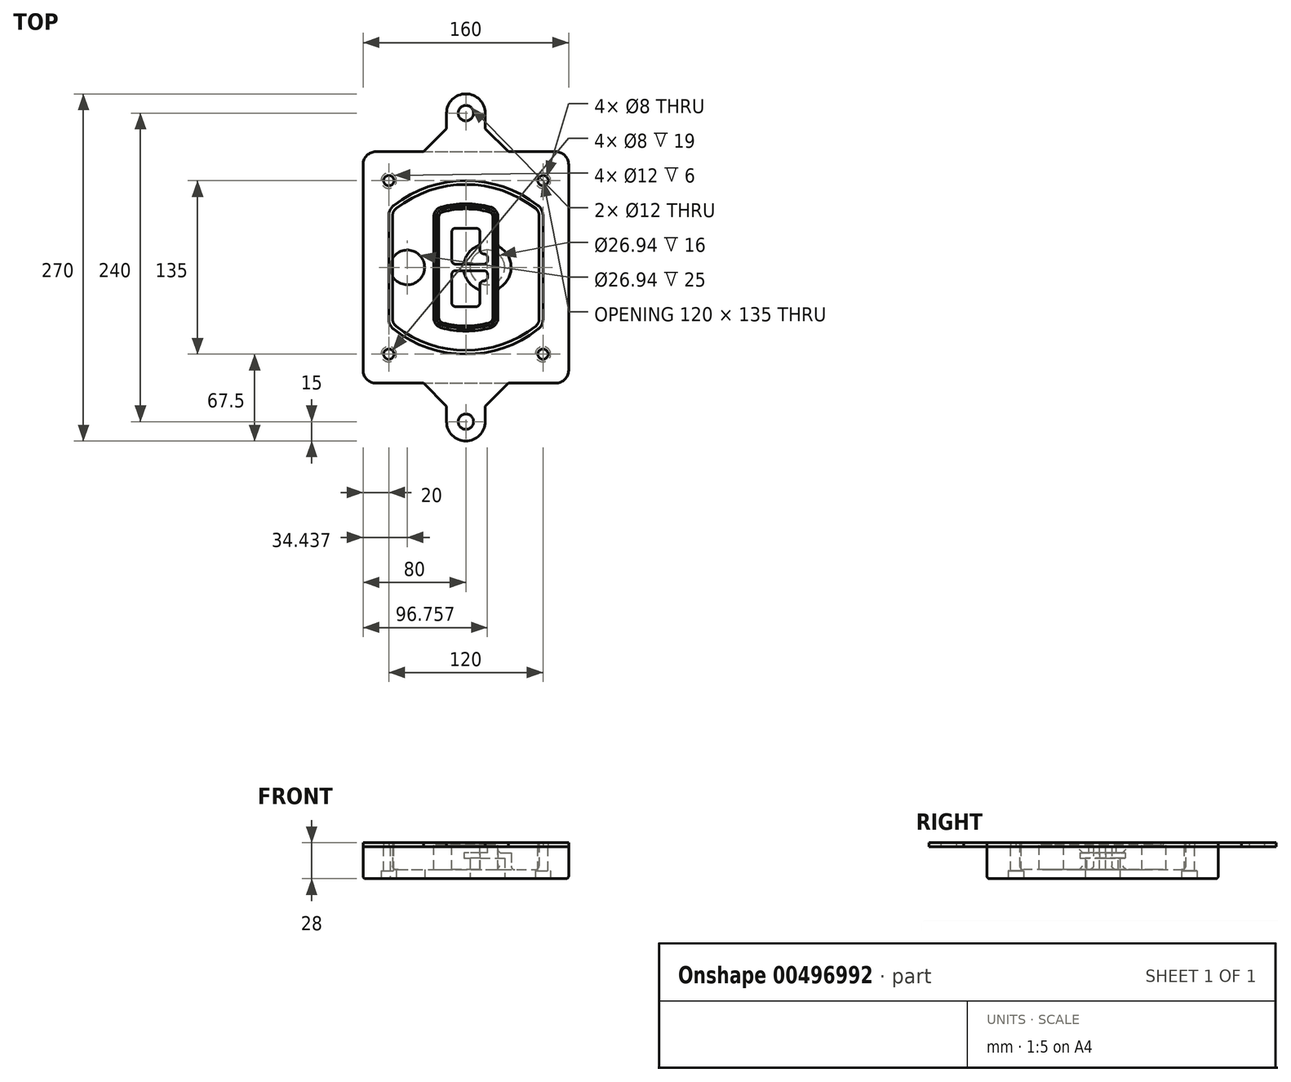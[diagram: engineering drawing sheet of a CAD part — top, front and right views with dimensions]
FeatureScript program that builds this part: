
annotation { "Feature Type Name" : "Feature", "Feature Type Description" : "" }
export const myFeature = defineFeature(function(context is Context, id is Id, definition is map)
    precondition{}
    {
        {
            var Q0;
            Q0=qCreatedBy(makeId("Top.planeOp"),FACE);
            var sketch = newSketch(context, id + "F0", { "sketchPlane" : qUnion([Q0])});
            skPoint(sketch, "E0.rect.middle", {"position": v(0, 0) * mm});
            skLineSegment(sketch, "E1.bottom", {"start": v(-70, -90) * mm, "end": v(70, -90) * mm});
            skLineSegment(sketch, "E1.top", {"start": v(-70, 90) * mm, "end": v(70, 90) * mm});
            skLineSegment(sketch, "E1.left", {"start": v(-80, -80) * mm, "end": v(-80, 80) * mm});
            skLineSegment(sketch, "E1.right", {"start": v(80, -80) * mm, "end": v(80, 80) * mm});
            skLineSegment(sketch, "E2", {"start": v(-80, 90) * mm, "end": v(80, -90) * mm, "construction": true});
            skLineSegment(sketch, "E3", {"start": v(80, 90) * mm, "end": v(-80, -90) * mm, "construction": true});
            skCircle(sketch, "E4", {"center": v(-60, 67.5) * mm, "radius": 4 * mm});
            skCircle(sketch, "E5", {"center": v(60, 67.5) * mm, "radius": 4 * mm});
            skCircle(sketch, "E6", {"center": v(60, -67.5) * mm, "radius": 4 * mm});
            skCircle(sketch, "E7", {"center": v(-60, -67.5) * mm, "radius": 4 * mm});
            skLineSegment(sketch, "E8", {"start": v(-60, 67.5) * mm, "end": v(60, 67.5) * mm, "construction": true});
            skLineSegment(sketch, "E9", {"start": v(60, 67.5) * mm, "end": v(60, -67.5) * mm, "construction": true});
            skLineSegment(sketch, "E10", {"start": v(60, -67.5) * mm, "end": v(-60, -67.5) * mm, "construction": true});
            skLineSegment(sketch, "E11", {"start": v(-60, -67.5) * mm, "end": v(-60, 67.5) * mm, "construction": true});
            skLineSegment(sketch, "E12", {"start": v(-60, 40.3) * mm, "end": v(-60, -40.3) * mm});
            skLineSegment(sketch, "E13", {"start": v(60, 40.3) * mm, "end": v(60, -40.3) * mm});
            skArc(sketch, "E14", {"start": v(56.15, 48.18) * mm, "mid": v(0, 67.5) * mm, "end": v(-56.15, 48.18) * mm});
            skArc(sketch, "E15", {"start": v(-56.15, -48.18) * mm, "mid": v(0, -67.5) * mm, "end": v(56.15, -48.18) * mm});
            skLineSegment(sketch, "E16", {"start": v(-60, 0) * mm, "end": v(60, 0) * mm, "construction": true});
            skPoint(sketch, "E17.visualSharp", {"position": v(-60, -45) * mm});
            skArc(sketch, "E17.filletArc", {"start": v(-60, -40.3) * mm, "mid": v(-58.99, -44.68) * mm, "end": v(-56.15, -48.18) * mm});
            skPoint(sketch, "E18.visualSharp", {"position": v(-60, 45) * mm});
            skArc(sketch, "E18.filletArc", {"start": v(-56.15, 48.18) * mm, "mid": v(-58.99, 44.68) * mm, "end": v(-60, 40.3) * mm});
            skPoint(sketch, "E19.visualSharp", {"position": v(60, 45) * mm});
            skArc(sketch, "E19.filletArc", {"start": v(60, 40.3) * mm, "mid": v(58.99, 44.68) * mm, "end": v(56.15, 48.18) * mm});
            skPoint(sketch, "E20.visualSharp", {"position": v(60, -45) * mm});
            skArc(sketch, "E20.filletArc", {"start": v(56.15, -48.18) * mm, "mid": v(58.99, -44.68) * mm, "end": v(60, -40.3) * mm});
            skPoint(sketch, "E21.visualSharp", {"position": v(-80, 90) * mm});
            skArc(sketch, "E21.filletArc", {"start": v(-70, 90) * mm, "mid": v(-77.07, 87.07) * mm, "end": v(-80, 80) * mm});
            skPoint(sketch, "E22.visualSharp", {"position": v(80, 90) * mm});
            skArc(sketch, "E22.filletArc", {"start": v(80, 80) * mm, "mid": v(77.07, 87.07) * mm, "end": v(70, 90) * mm});
            skPoint(sketch, "E23.visualSharp", {"position": v(80, -90) * mm});
            skArc(sketch, "E23.filletArc", {"start": v(70, -90) * mm, "mid": v(77.07, -87.07) * mm, "end": v(80, -80) * mm});
            skPoint(sketch, "E24.visualSharp", {"position": v(-80, -90) * mm});
            skArc(sketch, "E24.filletArc", {"start": v(-80, -80) * mm, "mid": v(-77.07, -87.07) * mm, "end": v(-70, -90) * mm});
            skArc(sketch, "E25.0", {"start": v(57, 40.3) * mm, "mid": v(56.3, 43.36) * mm, "end": v(54.3, 45.81) * mm});
            skLineSegment(sketch, "E25.1", {"start": v(57, 40.3) * mm, "end": v(57, -40.3) * mm});
            skArc(sketch, "E25.2", {"start": v(54.3, -45.81) * mm, "mid": v(56.3, -43.36) * mm, "end": v(57, -40.3) * mm});
            skArc(sketch, "E25.3", {"start": v(-54.3, -45.81) * mm, "mid": v(0, -64.5) * mm, "end": v(54.3, -45.81) * mm});
            skArc(sketch, "E25.4", {"start": v(-57, -40.3) * mm, "mid": v(-56.3, -43.36) * mm, "end": v(-54.3, -45.81) * mm});
            skArc(sketch, "E25.5", {"start": v(54.3, 45.81) * mm, "mid": v(0, 64.5) * mm, "end": v(-54.3, 45.81) * mm});
            skLineSegment(sketch, "E25.6", {"start": v(-57, 40.3) * mm, "end": v(-57, -40.3) * mm});
            skArc(sketch, "E25.7", {"start": v(-54.3, 45.81) * mm, "mid": v(-56.3, 43.36) * mm, "end": v(-57, 40.3) * mm});
            skArc(sketch, "E26.0", {"start": v(-58.62, 51.33) * mm, "mid": v(-62.58, 46.43) * mm, "end": v(-64, 40.3) * mm});
            skArc(sketch, "E26.1", {"start": v(58.62, 51.33) * mm, "mid": v(0, 71.5) * mm, "end": v(-58.62, 51.33) * mm});
            skArc(sketch, "E26.2", {"start": v(64, 40.3) * mm, "mid": v(62.58, 46.43) * mm, "end": v(58.62, 51.33) * mm});
            skLineSegment(sketch, "E26.3", {"start": v(64, 40.3) * mm, "end": v(64, -40.3) * mm});
            skArc(sketch, "E26.4", {"start": v(58.62, -51.33) * mm, "mid": v(62.58, -46.43) * mm, "end": v(64, -40.3) * mm});
            skLineSegment(sketch, "E26.5", {"start": v(-64, 40.3) * mm, "end": v(-64, -40.3) * mm});
            skArc(sketch, "E26.6", {"start": v(-58.62, -51.33) * mm, "mid": v(0, -71.5) * mm, "end": v(58.62, -51.33) * mm});
            skArc(sketch, "E26.7", {"start": v(-64, -40.3) * mm, "mid": v(-62.58, -46.43) * mm, "end": v(-58.62, -51.33) * mm});
            skSolve(sketch);
        }
        {
            var Q0;
            Q0=makeQuery(id+"F0.imprint","IMPRINT",FACE,{"disambiguationData":[TD([[makeQuery(id+"F0.imprint","IMPRINT",EDGE,{"derivedFrom":sQuery(id+"F0.wireOp",EDGE,"E1.bottom")}),1.0]])]});
            var Q1;
            Q1=makeQuery(id+"F0.imprint","IMPRINT",FACE,{"disambiguationData":[TD([[makeQuery(id+"F0.imprint","IMPRINT",EDGE,{"derivedFrom":sQuery(id+"F0.wireOp",EDGE,"E12")}),1.0]])]});
            var Q2;
            Q2=makeQuery(id+"F0.imprint","IMPRINT",FACE,{"disambiguationData":[TD([[makeQuery(id+"F0.imprint","IMPRINT",EDGE,{"derivedFrom":sQuery(id+"F0.wireOp",EDGE,"E25.0")}),1.0]])]});
            var Q3;
            Q3=makeQuery(id+"F0.imprint","IMPRINT",FACE,{"disambiguationData":[TD([[makeQuery(id+"F0.imprint","IMPRINT",EDGE,{"derivedFrom":sQuery(id+"F0.wireOp",EDGE,"E12")}),-1.0]])]});
            extrude(context, id + "F1", {"entities" : qUnion([Q0, Q1, Q2, Q3]), "oppositeDirection" : true, "depth" : 25 * mm});
        }
        {
            var Q0;
            Q0=makeQuery(id+"F0.imprint","IMPRINT",FACE,{"disambiguationData":[TD([[makeQuery(id+"F0.imprint","IMPRINT",EDGE,{"derivedFrom":sQuery(id+"F0.wireOp",EDGE,"E12")}),1.0]])]});
            extrude(context, id + "F2", {"entities" : qUnion([Q0]), "operationType" : NewBodyOperationType.ADD, "depth" : 3 * mm});
        }
        {
            var Q0;
            Q0=makeQuery(id+"F0.imprint","IMPRINT",FACE,{"disambiguationData":[TD([[makeQuery(id+"F0.imprint","IMPRINT",EDGE,{"derivedFrom":sQuery(id+"F0.wireOp",EDGE,"E25.0")}),1.0]])]});
            extrude(context, id + "F3", {"entities" : qUnion([Q0]), "operationType" : NewBodyOperationType.REMOVE, "oppositeDirection" : true, "depth" : 18 * mm});
        }
        {
            var Q0;
            Q0=makeQuery(id+"F2.opExtrude","CAP_FACE",FACE,{"disambiguationData":[OSD([sQuery(id+"F0.wireOp",EDGE,"E12"),sQuery(id+"F0.wireOp",EDGE,"E13"),sQuery(id+"F0.wireOp",EDGE,"E14"),sQuery(id+"F0.wireOp",EDGE,"E15"),sQuery(id+"F0.wireOp",EDGE,"E17.filletArc"),sQuery(id+"F0.wireOp",EDGE,"E18.filletArc"),sQuery(id+"F0.wireOp",EDGE,"E19.filletArc"),sQuery(id+"F0.wireOp",EDGE,"E20.filletArc"),sQuery(id+"F0.wireOp",EDGE,"E25.0"),sQuery(id+"F0.wireOp",EDGE,"E25.1"),sQuery(id+"F0.wireOp",EDGE,"E25.2"),sQuery(id+"F0.wireOp",EDGE,"E25.3"),sQuery(id+"F0.wireOp",EDGE,"E25.4"),sQuery(id+"F0.wireOp",EDGE,"E25.5"),sQuery(id+"F0.wireOp",EDGE,"E25.6"),sQuery(id+"F0.wireOp",EDGE,"E25.7")])],"isStart":false});
            var sketch = newSketch(context, id + "F4", { "sketchPlane" : qUnion([Q0])});
            skArc(sketch, "E27.0", {"start": v(-19.08, -46.97) * mm, "mid": v(0, -49.5) * mm, "end": v(19.08, -46.97) * mm});
            skArc(sketch, "E28.0", {"start": v(19.08, 46.97) * mm, "mid": v(0, 49.5) * mm, "end": v(-19.08, 46.97) * mm});
            skLineSegment(sketch, "E29", {"start": v(-25, 39.25) * mm, "end": v(-25, -39.25) * mm});
            skLineSegment(sketch, "E30", {"start": v(25, 39.25) * mm, "end": v(25, -39.25) * mm});
            skLineSegment(sketch, "E31", {"start": v(-25, 45.1) * mm, "end": v(25, 45.1) * mm, "construction": true});
            skLineSegment(sketch, "E32", {"start": v(-25, -45.1) * mm, "end": v(25, -45.1) * mm, "construction": true});
            skPoint(sketch, "E33.visualSharp", {"position": v(-25, 45.1) * mm});
            skArc(sketch, "E33.filletArc", {"start": v(-19.08, 46.97) * mm, "mid": v(-23.35, 44.11) * mm, "end": v(-25, 39.25) * mm});
            skPoint(sketch, "E34.visualSharp", {"position": v(25, 45.1) * mm});
            skArc(sketch, "E34.filletArc", {"start": v(25, 39.25) * mm, "mid": v(23.35, 44.11) * mm, "end": v(19.08, 46.97) * mm});
            skPoint(sketch, "E35.visualSharp", {"position": v(25, -45.1) * mm});
            skArc(sketch, "E35.filletArc", {"start": v(19.08, -46.97) * mm, "mid": v(23.35, -44.11) * mm, "end": v(25, -39.25) * mm});
            skPoint(sketch, "E36.visualSharp", {"position": v(-25, -45.1) * mm});
            skArc(sketch, "E36.filletArc", {"start": v(-25, -39.25) * mm, "mid": v(-23.35, -44.11) * mm, "end": v(-19.08, -46.97) * mm});
            skArc(sketch, "E37.0", {"start": v(54.3, 45.81) * mm, "mid": v(0, 64.5) * mm, "end": v(-54.3, 45.81) * mm});
            skArc(sketch, "E37.1", {"start": v(-54.3, 45.81) * mm, "mid": v(-56.3, 43.36) * mm, "end": v(-57, 40.3) * mm});
            skLineSegment(sketch, "E37.2", {"start": v(-57, 40.3) * mm, "end": v(-57, -40.3) * mm});
            skArc(sketch, "E37.3", {"start": v(-57, -40.3) * mm, "mid": v(-56.3, -43.36) * mm, "end": v(-54.3, -45.81) * mm});
            skArc(sketch, "E37.4", {"start": v(-54.3, -45.81) * mm, "mid": v(0, -64.5) * mm, "end": v(54.3, -45.81) * mm});
            skArc(sketch, "E37.5", {"start": v(54.3, -45.81) * mm, "mid": v(56.3, -43.36) * mm, "end": v(57, -40.3) * mm});
            skLineSegment(sketch, "E37.6", {"start": v(57, 40.3) * mm, "end": v(57, -40.3) * mm});
            skArc(sketch, "E37.7", {"start": v(57, 40.3) * mm, "mid": v(56.3, 43.36) * mm, "end": v(54.3, 45.81) * mm});
            skLineSegment(sketch, "E38.0", {"start": v(23, 39.25) * mm, "end": v(23, -39.25) * mm});
            skArc(sketch, "E38.1", {"start": v(18.56, -45.04) * mm, "mid": v(21.76, -42.9) * mm, "end": v(23, -39.25) * mm});
            skArc(sketch, "E38.2", {"start": v(-18.56, -45.04) * mm, "mid": v(0, -47.5) * mm, "end": v(18.56, -45.04) * mm});
            skArc(sketch, "E38.3", {"start": v(-23, -39.25) * mm, "mid": v(-21.76, -42.9) * mm, "end": v(-18.56, -45.04) * mm});
            skLineSegment(sketch, "E38.4", {"start": v(-23, 39.25) * mm, "end": v(-23, -39.25) * mm});
            skArc(sketch, "E38.5", {"start": v(23, 39.25) * mm, "mid": v(21.76, 42.9) * mm, "end": v(18.56, 45.04) * mm});
            skArc(sketch, "E38.6", {"start": v(-18.56, 45.04) * mm, "mid": v(-21.76, 42.9) * mm, "end": v(-23, 39.25) * mm});
            skArc(sketch, "E38.7", {"start": v(18.56, 45.04) * mm, "mid": v(0, 47.5) * mm, "end": v(-18.56, 45.04) * mm});
            skArc(sketch, "E39.0", {"start": v(21, 39.25) * mm, "mid": v(20.18, 41.68) * mm, "end": v(18.04, 43.1) * mm});
            skLineSegment(sketch, "E39.1", {"start": v(21, 39.25) * mm, "end": v(21, -39.25) * mm});
            skArc(sketch, "E39.2", {"start": v(18.04, -43.1) * mm, "mid": v(20.18, -41.68) * mm, "end": v(21, -39.25) * mm});
            skArc(sketch, "E39.3", {"start": v(-18.04, -43.1) * mm, "mid": v(0, -45.5) * mm, "end": v(18.04, -43.1) * mm});
            skArc(sketch, "E39.4", {"start": v(-21, -39.25) * mm, "mid": v(-20.18, -41.68) * mm, "end": v(-18.04, -43.1) * mm});
            skArc(sketch, "E39.5", {"start": v(18.04, 43.1) * mm, "mid": v(0, 45.5) * mm, "end": v(-18.04, 43.1) * mm});
            skLineSegment(sketch, "E39.6", {"start": v(-21, 39.25) * mm, "end": v(-21, -39.25) * mm});
            skArc(sketch, "E39.7", {"start": v(-18.04, 43.1) * mm, "mid": v(-20.18, 41.68) * mm, "end": v(-21, 39.25) * mm});
            skLineSegment(sketch, "E40", {"start": v(-25, 0) * mm, "end": v(25, 0) * mm, "construction": true});
            skLineSegment(sketch, "E41", {"start": v(-11, 5.5) * mm, "end": v(-11, 27.5) * mm});
            skLineSegment(sketch, "E42", {"start": v(-8, 30.5) * mm, "end": v(8, 30.5) * mm});
            skLineSegment(sketch, "E43", {"start": v(11, 27.5) * mm, "end": v(11, 13.5) * mm});
            skLineSegment(sketch, "E44", {"start": v(14, 10.5) * mm, "end": v(14, 10.5) * mm});
            skLineSegment(sketch, "E45", {"start": v(17, 7.5) * mm, "end": v(17, 5.5) * mm});
            skLineSegment(sketch, "E46", {"start": v(14, 2.5) * mm, "end": v(-8, 2.5) * mm});
            skPoint(sketch, "E47.visualSharp", {"position": v(-11, 30.5) * mm});
            skArc(sketch, "E47.filletArc", {"start": v(-8, 30.5) * mm, "mid": v(-10.12, 29.62) * mm, "end": v(-11, 27.5) * mm});
            skPoint(sketch, "E48.visualSharp", {"position": v(11, 30.5) * mm});
            skArc(sketch, "E48.filletArc", {"start": v(11, 27.5) * mm, "mid": v(10.12, 29.62) * mm, "end": v(8, 30.5) * mm});
            skPoint(sketch, "E49.visualSharp", {"position": v(11, 10.5) * mm});
            skArc(sketch, "E49.filletArc", {"start": v(11, 13.5) * mm, "mid": v(11.88, 11.38) * mm, "end": v(14, 10.5) * mm});
            skPoint(sketch, "E50.visualSharp", {"position": v(17, 10.5) * mm});
            skArc(sketch, "E50.filletArc", {"start": v(17, 7.5) * mm, "mid": v(16.12, 9.62) * mm, "end": v(14, 10.5) * mm});
            skPoint(sketch, "E51.visualSharp", {"position": v(17, 2.5) * mm});
            skArc(sketch, "E51.filletArc", {"start": v(14, 2.5) * mm, "mid": v(16.12, 3.38) * mm, "end": v(17, 5.5) * mm});
            skPoint(sketch, "E52.visualSharp", {"position": v(-11, 2.5) * mm});
            skArc(sketch, "E52.filletArc", {"start": v(-11, 5.5) * mm, "mid": v(-10.12, 3.38) * mm, "end": v(-8, 2.5) * mm});
            skLineSegment(sketch, "E53.0.MirrorCS", {"start": v(14, -2.5) * mm, "end": v(-8, -2.5) * mm});
            skArc(sketch, "E54.0.MirrorCS", {"start": v(-11, -5.5) * mm, "mid": v(-10.12, -3.38) * mm, "end": v(-8, -2.5) * mm});
            skLineSegment(sketch, "E55.0.MirrorCS", {"start": v(-11, -5.5) * mm, "end": v(-11, -27.5) * mm});
            skArc(sketch, "E56.0.MirrorCS", {"start": v(-8, -30.5) * mm, "mid": v(-10.12, -29.62) * mm, "end": v(-11, -27.5) * mm});
            skLineSegment(sketch, "E57.0.MirrorCS", {"start": v(-8, -30.5) * mm, "end": v(8, -30.5) * mm});
            skArc(sketch, "E58.0.MirrorCS", {"start": v(11, -27.5) * mm, "mid": v(10.12, -29.62) * mm, "end": v(8, -30.5) * mm});
            skLineSegment(sketch, "E59.0.MirrorCS", {"start": v(11, -27.5) * mm, "end": v(11, -13.5) * mm});
            skArc(sketch, "E60.0.MirrorCS", {"start": v(11, -13.5) * mm, "mid": v(11.88, -11.38) * mm, "end": v(14, -10.5) * mm});
            skArc(sketch, "E61.0.MirrorCS", {"start": v(17, -7.5) * mm, "mid": v(16.12, -9.62) * mm, "end": v(14, -10.5) * mm});
            skLineSegment(sketch, "E62.0.MirrorCS", {"start": v(17, -7.5) * mm, "end": v(17, -5.5) * mm});
            skArc(sketch, "E63.0.MirrorCS", {"start": v(14, -2.5) * mm, "mid": v(16.12, -3.38) * mm, "end": v(17, -5.5) * mm});
            skSolve(sketch);
        }
        {
            var Q0;
            Q0=makeQuery(id+"F4.imprint","IMPRINT",FACE,{"disambiguationData":[TD([[makeQuery(id+"F4.imprint","IMPRINT",EDGE,{"derivedFrom":sQuery(id+"F4.wireOp",EDGE,"E27.0")}),1.0]])]});
            var Q1;
            Q1=makeQuery(id+"F4.imprint","IMPRINT",FACE,{"disambiguationData":[TD([[makeQuery(id+"F4.imprint","IMPRINT",EDGE,{"derivedFrom":sQuery(id+"F4.wireOp",EDGE,"E38.0")}),-1.0]])]});
            var Q2;
            Q2=makeQuery(id+"F4.imprint","IMPRINT",FACE,{"disambiguationData":[TD([[makeQuery(id+"F4.imprint","IMPRINT",EDGE,{"derivedFrom":sQuery(id+"F4.wireOp",EDGE,"E39.0")}),1.0]])]});
            extrude(context, id + "F5", {"entities" : qUnion([Q0, Q1, Q2]), "operationType" : NewBodyOperationType.ADD, "endBound" : BoundingType.UP_TO_NEXT, "oppositeDirection" : true, "depth" : 25 * mm});
        }
        {
            var Q0;
            Q0=makeQuery(id+"F4.imprint","IMPRINT",FACE,{"disambiguationData":[TD([[makeQuery(id+"F4.imprint","IMPRINT",EDGE,{"derivedFrom":sQuery(id+"F4.wireOp",EDGE,"E38.0")}),-1.0]])]});
            extrude(context, id + "F6", {"entities" : qUnion([Q0]), "operationType" : NewBodyOperationType.REMOVE, "oppositeDirection" : true, "depth" : 2 * mm});
        }
        {
            var Q0;
            Q0=makeQuery(id+"F1.opExtrude","CAP_FACE",FACE,{"disambiguationData":[OSD([sQuery(id+"F0.wireOp",EDGE,"E1.bottom"),sQuery(id+"F0.wireOp",EDGE,"E1.top"),sQuery(id+"F0.wireOp",EDGE,"E1.left"),sQuery(id+"F0.wireOp",EDGE,"E1.right"),sQuery(id+"F0.wireOp",EDGE,"E4"),sQuery(id+"F0.wireOp",EDGE,"E5"),sQuery(id+"F0.wireOp",EDGE,"E6"),sQuery(id+"F0.wireOp",EDGE,"E7"),sQuery(id+"F0.wireOp",EDGE,"E21.filletArc"),sQuery(id+"F0.wireOp",EDGE,"E22.filletArc"),sQuery(id+"F0.wireOp",EDGE,"E23.filletArc"),sQuery(id+"F0.wireOp",EDGE,"E24.filletArc")])],"isStart":false});
            var sketch = newSketch(context, id + "F7", { "sketchPlane" : qUnion([Q0])});
            skCircle(sketch, "E64", {"center": v(16.76, 0) * mm, "radius": 13.47 * mm});
            skCircle(sketch, "E65", {"center": v(-45.56, 0) * mm, "radius": 13.47 * mm});
            skLineSegment(sketch, "E66", {"start": v(80, 0) * mm, "end": v(-80, 0) * mm});
            skCircle(sketch, "E67", {"center": v(16.76, 0) * mm, "radius": 18.47 * mm});
            skCircle(sketch, "E68", {"center": v(60, -67.5) * mm, "radius": 6 * mm});
            skCircle(sketch, "E69", {"center": v(-60, -67.5) * mm, "radius": 6 * mm});
            skCircle(sketch, "E70", {"center": v(-60, 67.5) * mm, "radius": 6 * mm});
            skCircle(sketch, "E71", {"center": v(60, 67.5) * mm, "radius": 6 * mm});
            skSolve(sketch);
        }
        {
            var Q0;
            {var subQ1=sQuery(id+"F7.wireOp",EDGE,"E66");var subQ4=sQuery(id+"F7.wireOp",EDGE,"E64");var subQ6=makeQuery(id+"F7.imprint","INTERSECT",VERTEX,{"disambiguationData":[OD(0.0)],"derivedFrom":[subQ4,subQ1]});Q0=makeQuery(id+"F7.imprint","IMPRINT",FACE,{"disambiguationData":[TD([[makeQuery(id+"F7.imprint","IMPRINT",EDGE,{"disambiguationData":[TD([[subQ6,-1.0]])],"derivedFrom":subQ4}),-1.0]])]});}
            var Q1;
            {var subQ0=sQuery(id+"F7.wireOp",EDGE,"E66");var subQ1=sQuery(id+"F7.wireOp",EDGE,"E64");var subQ3=makeQuery(id+"F7.imprint","INTERSECT",VERTEX,{"disambiguationData":[OD(0.0)],"derivedFrom":[subQ1,subQ0]});Q1=makeQuery(id+"F7.imprint","IMPRINT",FACE,{"disambiguationData":[TD([[makeQuery(id+"F7.imprint","IMPRINT",EDGE,{"disambiguationData":[TD([[subQ3,-1.0]])],"derivedFrom":subQ1}),1.0]])]});}
            var Q2;
            {var subQ0=sQuery(id+"F7.wireOp",EDGE,"E66");var subQ1=sQuery(id+"F7.wireOp",EDGE,"E64");var subQ3=makeQuery(id+"F7.imprint","INTERSECT",VERTEX,{"disambiguationData":[OD(0.0)],"derivedFrom":[subQ1,subQ0]});Q2=makeQuery(id+"F7.imprint","IMPRINT",FACE,{"disambiguationData":[TD([[makeQuery(id+"F7.imprint","IMPRINT",EDGE,{"disambiguationData":[TD([[subQ3,1.0]])],"derivedFrom":subQ1}),1.0]])]});}
            var Q3;
            {var subQ1=sQuery(id+"F7.wireOp",EDGE,"E66");var subQ4=sQuery(id+"F7.wireOp",EDGE,"E64");var subQ6=makeQuery(id+"F7.imprint","INTERSECT",VERTEX,{"disambiguationData":[OD(0.0)],"derivedFrom":[subQ4,subQ1]});Q3=makeQuery(id+"F7.imprint","IMPRINT",FACE,{"disambiguationData":[TD([[makeQuery(id+"F7.imprint","IMPRINT",EDGE,{"disambiguationData":[TD([[subQ6,1.0]])],"derivedFrom":subQ4}),-1.0]])]});}
            extrude(context, id + "F8", {"entities" : qUnion([Q0, Q1, Q2, Q3]), "operationType" : NewBodyOperationType.ADD, "oppositeDirection" : true, "depth" : 20 * mm});
        }
        {
            var Q0;
            {var subQ0=sQuery(id+"F7.wireOp",EDGE,"E66");var subQ1=sQuery(id+"F7.wireOp",EDGE,"E64");var subQ3=makeQuery(id+"F7.imprint","INTERSECT",VERTEX,{"disambiguationData":[OD(0.0)],"derivedFrom":[subQ1,subQ0]});Q0=makeQuery(id+"F7.imprint","IMPRINT",FACE,{"disambiguationData":[TD([[makeQuery(id+"F7.imprint","IMPRINT",EDGE,{"disambiguationData":[TD([[subQ3,-1.0]])],"derivedFrom":subQ1}),1.0]])]});}
            var Q1;
            {var subQ0=sQuery(id+"F7.wireOp",EDGE,"E66");var subQ1=sQuery(id+"F7.wireOp",EDGE,"E64");var subQ3=makeQuery(id+"F7.imprint","INTERSECT",VERTEX,{"disambiguationData":[OD(0.0)],"derivedFrom":[subQ1,subQ0]});Q1=makeQuery(id+"F7.imprint","IMPRINT",FACE,{"disambiguationData":[TD([[makeQuery(id+"F7.imprint","IMPRINT",EDGE,{"disambiguationData":[TD([[subQ3,1.0]])],"derivedFrom":subQ1}),1.0]])]});}
            extrude(context, id + "F9", {"entities" : qUnion([Q0, Q1]), "operationType" : NewBodyOperationType.REMOVE, "oppositeDirection" : true, "depth" : 16 * mm});
        }
        {
            var Q0;
            {var subQ0=sQuery(id+"F7.wireOp",EDGE,"E66");var subQ1=sQuery(id+"F7.wireOp",EDGE,"E65");var subQ3=makeQuery(id+"F7.imprint","INTERSECT",VERTEX,{"disambiguationData":[OD(0.0)],"derivedFrom":[subQ1,subQ0]});Q0=makeQuery(id+"F7.imprint","IMPRINT",FACE,{"disambiguationData":[TD([[makeQuery(id+"F7.imprint","IMPRINT",EDGE,{"disambiguationData":[TD([[subQ3,-1.0]])],"derivedFrom":subQ1}),1.0]])]});}
            var Q1;
            {var subQ0=sQuery(id+"F7.wireOp",EDGE,"E66");var subQ1=sQuery(id+"F7.wireOp",EDGE,"E65");var subQ3=makeQuery(id+"F7.imprint","INTERSECT",VERTEX,{"disambiguationData":[OD(0.0)],"derivedFrom":[subQ1,subQ0]});Q1=makeQuery(id+"F7.imprint","IMPRINT",FACE,{"disambiguationData":[TD([[makeQuery(id+"F7.imprint","IMPRINT",EDGE,{"disambiguationData":[TD([[subQ3,1.0]])],"derivedFrom":subQ1}),1.0]])]});}
            extrude(context, id + "F10", {"entities" : qUnion([Q0, Q1]), "operationType" : NewBodyOperationType.REMOVE, "oppositeDirection" : true, "depth" : 25 * mm});
        }
        {
            var Q0;
            Q0=makeQuery(id+"F7.imprint","IMPRINT",FACE,{"disambiguationData":[TD([[makeQuery(id+"F7.imprint","IMPRINT",EDGE,{"derivedFrom":sQuery(id+"F7.wireOp",EDGE,"E68")}),1.0]])]});
            var Q1;
            Q1=makeQuery(id+"F7.imprint","IMPRINT",FACE,{"disambiguationData":[TD([[makeQuery(id+"F7.imprint","IMPRINT",EDGE,{"derivedFrom":makeQuery(id+"F1.opExtrude","CAP_EDGE",EDGE,{"disambiguationData":[OSD([sQuery(id+"F0.wireOp",EDGE,"E5")])],"isStart":false})}),-1.0]])]});
            var Q2;
            Q2=makeQuery(id+"F7.imprint","IMPRINT",FACE,{"disambiguationData":[TD([[makeQuery(id+"F7.imprint","IMPRINT",EDGE,{"derivedFrom":sQuery(id+"F7.wireOp",EDGE,"E69")}),1.0]])]});
            var Q3;
            Q3=makeQuery(id+"F7.imprint","IMPRINT",FACE,{"disambiguationData":[TD([[makeQuery(id+"F7.imprint","IMPRINT",EDGE,{"derivedFrom":makeQuery(id+"F1.opExtrude","CAP_EDGE",EDGE,{"disambiguationData":[OSD([sQuery(id+"F0.wireOp",EDGE,"E4")])],"isStart":false})}),-1.0]])]});
            var Q4;
            Q4=makeQuery(id+"F7.imprint","IMPRINT",FACE,{"disambiguationData":[TD([[makeQuery(id+"F7.imprint","IMPRINT",EDGE,{"derivedFrom":sQuery(id+"F7.wireOp",EDGE,"E70")}),1.0]])]});
            var Q5;
            Q5=makeQuery(id+"F7.imprint","IMPRINT",FACE,{"disambiguationData":[TD([[makeQuery(id+"F7.imprint","IMPRINT",EDGE,{"derivedFrom":makeQuery(id+"F1.opExtrude","CAP_EDGE",EDGE,{"disambiguationData":[OSD([sQuery(id+"F0.wireOp",EDGE,"E7")])],"isStart":false})}),-1.0]])]});
            var Q6;
            Q6=makeQuery(id+"F7.imprint","IMPRINT",FACE,{"disambiguationData":[TD([[makeQuery(id+"F7.imprint","IMPRINT",EDGE,{"derivedFrom":sQuery(id+"F7.wireOp",EDGE,"E71")}),1.0]])]});
            var Q7;
            Q7=makeQuery(id+"F7.imprint","IMPRINT",FACE,{"disambiguationData":[TD([[makeQuery(id+"F7.imprint","IMPRINT",EDGE,{"derivedFrom":makeQuery(id+"F1.opExtrude","CAP_EDGE",EDGE,{"disambiguationData":[OSD([sQuery(id+"F0.wireOp",EDGE,"E6")])],"isStart":false})}),-1.0]])]});
            extrude(context, id + "F11", {"entities" : qUnion([Q0, Q1, Q2, Q3, Q4, Q5, Q6, Q7]), "operationType" : NewBodyOperationType.REMOVE, "oppositeDirection" : true, "depth" : 6 * mm});
        }
        {
            var Q0;
            Q0=makeQuery(id+"F9.boolean.opBoolean","COPY",FACE,{"derivedFrom":makeQuery(id+"F9.opExtrude","CAP_FACE",FACE,{"disambiguationData":[OSD([sQuery(id+"F7.wireOp",EDGE,"E64")])],"isStart":false})});
            var sketch = newSketch(context, id + "F12", { "sketchPlane" : qUnion([Q0])});
            skArc(sketch, "E72.0", {"start": v(11, 17.55) * mm, "mid": v(2.57, 11.82) * mm, "end": v(-1.54, 2.5) * mm});
            skArc(sketch, "E72.1", {"start": v(-1.54, -2.5) * mm, "mid": v(2.57, -11.82) * mm, "end": v(11, -17.55) * mm});
            skLineSegment(sketch, "E73", {"start": v(-1.54, -2.5) * mm, "end": v(14, -2.5) * mm});
            skLineSegment(sketch, "E74.0", {"start": v(14, 2.5) * mm, "end": v(-1.54, 2.5) * mm});
            skArc(sketch, "E74.1", {"start": v(14, 2.5) * mm, "mid": v(16.12, 3.38) * mm, "end": v(17, 5.5) * mm});
            skLineSegment(sketch, "E74.2", {"start": v(17, 7.5) * mm, "end": v(17, 5.5) * mm});
            skArc(sketch, "E74.3", {"start": v(17, 7.5) * mm, "mid": v(16.12, 9.62) * mm, "end": v(14, 10.5) * mm});
            skArc(sketch, "E74.4", {"start": v(11, 13.5) * mm, "mid": v(11.88, 11.38) * mm, "end": v(14, 10.5) * mm});
            skLineSegment(sketch, "E74.5", {"start": v(11, 17.55) * mm, "end": v(11, 13.5) * mm});
            skLineSegment(sketch, "E74.7", {"start": v(14, -2.5) * mm, "end": v(-1.54, -2.5) * mm});
            skArc(sketch, "E74.8", {"start": v(14, -2.5) * mm, "mid": v(16.12, -3.38) * mm, "end": v(17, -5.5) * mm});
            skLineSegment(sketch, "E74.9", {"start": v(17, -7.5) * mm, "end": v(17, -5.5) * mm});
            skArc(sketch, "E74.10", {"start": v(17, -7.5) * mm, "mid": v(16.12, -9.62) * mm, "end": v(14, -10.5) * mm});
            skArc(sketch, "E74.11", {"start": v(11, -13.5) * mm, "mid": v(11.88, -11.38) * mm, "end": v(14, -10.5) * mm});
            skLineSegment(sketch, "E74.12", {"start": v(11, -17.55) * mm, "end": v(11, -13.5) * mm});
            skPoint(sketch, "E75.orphan", {"position": v(11, -27.5) * mm});
            skPoint(sketch, "E76.orphan", {"position": v(-8, -2.5) * mm});
            skPoint(sketch, "E77.orphan", {"position": v(-8, 2.5) * mm});
            skPoint(sketch, "E78.orphan", {"position": v(11, 27.5) * mm});
            skSolve(sketch);
        }
        {
            var Q0;
            {var subQ7=sQuery(id+"F12.wireOp",EDGE,"E72.0");var subQ14=sQuery(id+"F12.wireOp",EDGE,"E72.1");var subQ16=sQuery(id+"F12.wireOp",EDGE,"E74.1");var subQ18=sQuery(id+"F12.wireOp",EDGE,"E74.8");Q0=qUnion([makeQuery(id+"F12.imprint","IMPRINT",FACE,{"disambiguationData":[TD([[makeQuery(id+"F12.imprint","IMPRINT",EDGE,{"derivedFrom":subQ7}),1.0]])]}),makeQuery(id+"F12.imprint","IMPRINT",FACE,{"disambiguationData":[TD([[makeQuery(id+"F12.imprint","IMPRINT",EDGE,{"derivedFrom":subQ14}),1.0]])]}),makeQuery(id+"F12.imprint","IMPRINT",FACE,{"disambiguationData":[TD([[makeQuery(id+"F12.imprint","IMPRINT",EDGE,{"derivedFrom":subQ16}),1.0]])]}),makeQuery(id+"F12.imprint","IMPRINT",FACE,{"disambiguationData":[TD([[makeQuery(id+"F12.imprint","IMPRINT",EDGE,{"derivedFrom":subQ18}),-1.0]])]})]);}
            var Q1;
            Q1=makeQuery(id+"F5.boolean.opBoolean","SPLIT",FACE,{"disambiguationData":[TD([makeQuery(id+"F5.opExtrude","SWEPT_FACE",FACE,{"disambiguationData":[OSD([sQuery(id+"F4.wireOp",EDGE,"E41")])]})])],"derivedFrom":makeQuery(id+"F3.boolean.opBoolean","COPY",FACE,{"derivedFrom":makeQuery(id+"F3.opExtrude","CAP_FACE",FACE,{"disambiguationData":[OSD([sQuery(id+"F0.wireOp",EDGE,"E25.0"),sQuery(id+"F0.wireOp",EDGE,"E25.1"),sQuery(id+"F0.wireOp",EDGE,"E25.2"),sQuery(id+"F0.wireOp",EDGE,"E25.3"),sQuery(id+"F0.wireOp",EDGE,"E25.4"),sQuery(id+"F0.wireOp",EDGE,"E25.5"),sQuery(id+"F0.wireOp",EDGE,"E25.6"),sQuery(id+"F0.wireOp",EDGE,"E25.7")])],"isStart":false})})});
            extrude(context, id + "F13", {"entities" : qUnion([Q0]), "operationType" : NewBodyOperationType.REMOVE, "endBound" : BoundingType.UP_TO_SURFACE, "endBoundEntityFace" : qUnion([Q1]), "depth" : 25 * mm});
        }
        {
            var Q0;
            Q0=makeQuery(id+"F3.boolean.opBoolean","COPY",EDGE,{"derivedFrom":makeQuery(id+"F3.opExtrude","CAP_EDGE",EDGE,{"disambiguationData":[OSD([sQuery(id+"F0.wireOp",EDGE,"E25.6")])],"isStart":false})});
            var Q1;
            Q1=makeQuery(id+"F8.boolean.opBoolean","INTERSECT",EDGE,{"derivedFrom":[makeQuery(id+"F5.opExtrude","SWEPT_FACE",FACE,{"disambiguationData":[OSD([sQuery(id+"F4.wireOp",EDGE,"E30")])]}),makeQuery(id+"F8.opExtrude","CAP_FACE",FACE,{"disambiguationData":[OSD([sQuery(id+"F7.wireOp",EDGE,"E67")])],"isStart":false})]});
            var Q2;
            Q2=makeQuery(id+"F8.boolean.opBoolean","INTERSECT",EDGE,{"disambiguationData":[OD(1.0)],"derivedFrom":[makeQuery(id+"F5.opExtrude","SWEPT_FACE",FACE,{"disambiguationData":[OSD([sQuery(id+"F4.wireOp",EDGE,"E30")])]}),makeQuery(id+"F8.opExtrude","SWEPT_FACE",FACE,{"disambiguationData":[OSD([sQuery(id+"F7.wireOp",EDGE,"E67")])]})]});
            var Q3;
            {var subQ0=makeQuery(id+"F3.boolean.opBoolean","COPY",FACE,{"derivedFrom":makeQuery(id+"F3.opExtrude","CAP_FACE",FACE,{"disambiguationData":[OSD([sQuery(id+"F0.wireOp",EDGE,"E25.0"),sQuery(id+"F0.wireOp",EDGE,"E25.1"),sQuery(id+"F0.wireOp",EDGE,"E25.2"),sQuery(id+"F0.wireOp",EDGE,"E25.3"),sQuery(id+"F0.wireOp",EDGE,"E25.4"),sQuery(id+"F0.wireOp",EDGE,"E25.5"),sQuery(id+"F0.wireOp",EDGE,"E25.6"),sQuery(id+"F0.wireOp",EDGE,"E25.7")])],"isStart":false})});var subQ1=sQuery(id+"F4.wireOp",EDGE,"E30");Q3=makeQuery(id+"F8.boolean.opBoolean","SPLIT",EDGE,{"disambiguationData":[TD([makeQuery(id+"F5.opExtrude","SWEPT_FACE",FACE,{"disambiguationData":[OSD([sQuery(id+"F4.wireOp",EDGE,"E35.filletArc")])]})])],"derivedFrom":makeQuery(id+"F5.opExtrude","TWEAK_EDGE",EDGE,{"derivedFrom":[subQ0,makeQuery(id+"F4.imprint","IMPRINT",EDGE,{"derivedFrom":subQ1})]})});}
            var Q4;
            {var subQ0=sQuery(id+"F0.wireOp",EDGE,"E25.0");var subQ1=sQuery(id+"F0.wireOp",EDGE,"E25.1");var subQ2=sQuery(id+"F0.wireOp",EDGE,"E25.2");var subQ3=sQuery(id+"F0.wireOp",EDGE,"E25.3");var subQ4=sQuery(id+"F0.wireOp",EDGE,"E25.4");var subQ5=sQuery(id+"F0.wireOp",EDGE,"E25.5");var subQ6=sQuery(id+"F0.wireOp",EDGE,"E25.6");var subQ7=sQuery(id+"F0.wireOp",EDGE,"E25.7");Q4=makeQuery(id+"F8.boolean.opBoolean","INTERSECT",EDGE,{"derivedFrom":[makeQuery(id+"F5.boolean.opBoolean","SPLIT",FACE,{"disambiguationData":[TD([makeQuery(id+"F2.opExtrude","SWEPT_FACE",FACE,{"disambiguationData":[OSD([subQ0])]})])],"derivedFrom":makeQuery(id+"F3.boolean.opBoolean","COPY",FACE,{"derivedFrom":makeQuery(id+"F3.opExtrude","CAP_FACE",FACE,{"disambiguationData":[OSD([subQ0,subQ1,subQ2,subQ3,subQ4,subQ5,subQ6,subQ7])],"isStart":false})})}),makeQuery(id+"F8.opExtrude","SWEPT_FACE",FACE,{"disambiguationData":[OSD([sQuery(id+"F7.wireOp",EDGE,"E67")])]})]});}
            var Q5;
            Q5=makeQuery(id+"F8.boolean.opBoolean","INTERSECT",EDGE,{"disambiguationData":[OD(0.0)],"derivedFrom":[makeQuery(id+"F5.opExtrude","SWEPT_FACE",FACE,{"disambiguationData":[OSD([sQuery(id+"F4.wireOp",EDGE,"E30")])]}),makeQuery(id+"F8.opExtrude","SWEPT_FACE",FACE,{"disambiguationData":[OSD([sQuery(id+"F7.wireOp",EDGE,"E67")])]})]});
            fillet(context, id + "F14", {"entities" : qUnion([Q0, Q1, Q2, Q3, Q4, Q5]), "radius" : 3 * mm, "tangentPropagation" : true, "allowEdgeOverflow" : false});
        }
        {
            var Q0;
            Q0=makeQuery(id+"F1.opExtrude","CAP_EDGE",EDGE,{"disambiguationData":[OSD([sQuery(id+"F0.wireOp",EDGE,"E1.bottom")])],"isStart":false});
            fillet(context, id + "F15", {"entities" : qUnion([Q0]), "radius" : 2 * mm, "tangentPropagation" : true, "allowEdgeOverflow" : false});
        }
        {
            var Q0;
            {var subQ0=sQuery(id+"F0.wireOp",EDGE,"E21.filletArc");var subQ1=sQuery(id+"F0.wireOp",EDGE,"E7");var subQ2=sQuery(id+"F0.wireOp",EDGE,"E6");var subQ3=sQuery(id+"F0.wireOp",EDGE,"E5");var subQ4=sQuery(id+"F0.wireOp",EDGE,"E4");var subQ5=sQuery(id+"F0.wireOp",EDGE,"E22.filletArc");var subQ6=sQuery(id+"F0.wireOp",EDGE,"E1.bottom");var subQ7=sQuery(id+"F0.wireOp",EDGE,"E1.right");var subQ8=sQuery(id+"F0.wireOp",EDGE,"E1.top");var subQ9=sQuery(id+"F0.wireOp",EDGE,"E1.left");var subQ10=sQuery(id+"F0.wireOp",EDGE,"E23.filletArc");var subQ11=sQuery(id+"F0.wireOp",EDGE,"E24.filletArc");Q0=makeQuery(id+"F2.boolean.opBoolean","SPLIT",FACE,{"disambiguationData":[TD([makeQuery(id+"F1.opExtrude","SWEPT_FACE",FACE,{"disambiguationData":[OSD([subQ6])]})])],"derivedFrom":makeQuery(id+"F1.opExtrude","CAP_FACE",FACE,{"disambiguationData":[OSD([subQ6,subQ8,subQ9,subQ7,subQ4,subQ3,subQ2,subQ1,subQ0,subQ5,subQ10,subQ11])],"isStart":true})});}
            var sketch = newSketch(context, id + "F16", { "sketchPlane" : qUnion([Q0])});
            skLineSegment(sketch, "E79.0", {"start": v(-70, 90) * mm, "end": v(70, 90) * mm});
            skArc(sketch, "E80.0", {"start": v(80, 80) * mm, "mid": v(77.07, 87.07) * mm, "end": v(70, 90) * mm});
            skLineSegment(sketch, "E81.0", {"start": v(80, -80) * mm, "end": v(80, 80) * mm});
            skPoint(sketch, "E82.0", {"position": v(77.07, -87.07) * mm});
            skArc(sketch, "E83.0", {"start": v(70, -90) * mm, "mid": v(77.07, -87.07) * mm, "end": v(80, -80) * mm});
            skLineSegment(sketch, "E84.0", {"start": v(-70, -90) * mm, "end": v(70, -90) * mm});
            skArc(sketch, "E85.0", {"start": v(-80, -80) * mm, "mid": v(-77.07, -87.07) * mm, "end": v(-70, -90) * mm});
            skLineSegment(sketch, "E86.0", {"start": v(-80, -80) * mm, "end": v(-80, 80) * mm});
            skPoint(sketch, "E87.0", {"position": v(-77.07, 87.07) * mm});
            skArc(sketch, "E88.0", {"start": v(-70, 90) * mm, "mid": v(-77.07, 87.07) * mm, "end": v(-80, 80) * mm});
            skLineSegment(sketch, "E89", {"start": v(0, 90) * mm, "end": v(0, 0) * mm, "construction": true});
            skLineSegment(sketch, "E90", {"start": v(0, 90) * mm, "end": v(0, 120) * mm, "construction": true});
            skCircle(sketch, "E91", {"center": v(0, 120) * mm, "radius": 6 * mm});
            skArc(sketch, "E92", {"start": v(15, 120) * mm, "mid": v(0, 135) * mm, "end": v(-15, 120) * mm});
            skLineSegment(sketch, "E93", {"start": v(-15, 120) * mm, "end": v(-15, 108) * mm});
            skLineSegment(sketch, "E94", {"start": v(15, 120) * mm, "end": v(15, 108) * mm});
            skLineSegment(sketch, "E95", {"start": v(-15, 108) * mm, "end": v(-33, 90) * mm});
            skLineSegment(sketch, "E96", {"start": v(15, 108) * mm, "end": v(33, 90) * mm});
            skLineSegment(sketch, "E97", {"start": v(0, 0) * mm, "end": v(-80, 0) * mm, "construction": true});
            skLineSegment(sketch, "E98", {"start": v(-80, 0) * mm, "end": v(80, 0) * mm, "construction": true});
            skLineSegment(sketch, "E99.MirrorCS", {"start": v(0, -90) * mm, "end": v(0, 0) * mm, "construction": true});
            skLineSegment(sketch, "E100.MirrorCS", {"start": v(15, -108) * mm, "end": v(33, -90) * mm});
            skLineSegment(sketch, "E101.MirrorCS", {"start": v(-15, -108) * mm, "end": v(-33, -90) * mm});
            skLineSegment(sketch, "E102.MirrorCS", {"start": v(15, -120) * mm, "end": v(15, -108) * mm});
            skLineSegment(sketch, "E103.MirrorCS", {"start": v(-15, -120) * mm, "end": v(-15, -108) * mm});
            skArc(sketch, "E104.MirrorCS", {"start": v(15, -120) * mm, "mid": v(0, -135) * mm, "end": v(-15, -120) * mm});
            skCircle(sketch, "E105.MirrorC", {"center": v(0, -120) * mm, "radius": 6 * mm});
            skLineSegment(sketch, "E106.MirrorCS", {"start": v(0, -90) * mm, "end": v(0, -120) * mm, "construction": true});
            skSolve(sketch);
        }
        {
            var Q0;
            Q0=makeQuery(id+"F16.imprint","IMPRINT",FACE,{"disambiguationData":[TD([[makeQuery(id+"F16.imprint","IMPRINT",EDGE,{"derivedFrom":sQuery(id+"F16.wireOp",EDGE,"E91")}),-1.0]])]});
            var Q1;
            {var subQ1=sQuery(id+"F16.wireOp",EDGE,"E100.MirrorCS");Q1=makeQuery(id+"F16.imprint","IMPRINT",FACE,{"disambiguationData":[TD([[makeQuery(id+"F16.imprint","IMPRINT",EDGE,{"derivedFrom":subQ1}),1.0]])]});}
            var Q2;
            {var subQ4=sQuery(id+"F16.wireOp",EDGE,"E80.0");Q2=makeQuery(id+"F16.imprint","IMPRINT",FACE,{"disambiguationData":[TD([[makeQuery(id+"F16.imprint","IMPRINT",EDGE,{"derivedFrom":subQ4}),1.0]])]});}
            var Q3;
            Q3=makeQuery(id+"F2.opExtrude","CAP_FACE",FACE,{"disambiguationData":[OSD([sQuery(id+"F0.wireOp",EDGE,"E12"),sQuery(id+"F0.wireOp",EDGE,"E13"),sQuery(id+"F0.wireOp",EDGE,"E14"),sQuery(id+"F0.wireOp",EDGE,"E15"),sQuery(id+"F0.wireOp",EDGE,"E17.filletArc"),sQuery(id+"F0.wireOp",EDGE,"E18.filletArc"),sQuery(id+"F0.wireOp",EDGE,"E19.filletArc"),sQuery(id+"F0.wireOp",EDGE,"E20.filletArc"),sQuery(id+"F0.wireOp",EDGE,"E25.0"),sQuery(id+"F0.wireOp",EDGE,"E25.1"),sQuery(id+"F0.wireOp",EDGE,"E25.2"),sQuery(id+"F0.wireOp",EDGE,"E25.3"),sQuery(id+"F0.wireOp",EDGE,"E25.4"),sQuery(id+"F0.wireOp",EDGE,"E25.5"),sQuery(id+"F0.wireOp",EDGE,"E25.6"),sQuery(id+"F0.wireOp",EDGE,"E25.7")])],"isStart":false});
            extrude(context, id + "F17", {"entities" : qUnion([Q0, Q1, Q2]), "endBound" : BoundingType.UP_TO_SURFACE, "endBoundEntityFace" : qUnion([Q3]), "depth" : 25 * mm});
        }
    });
